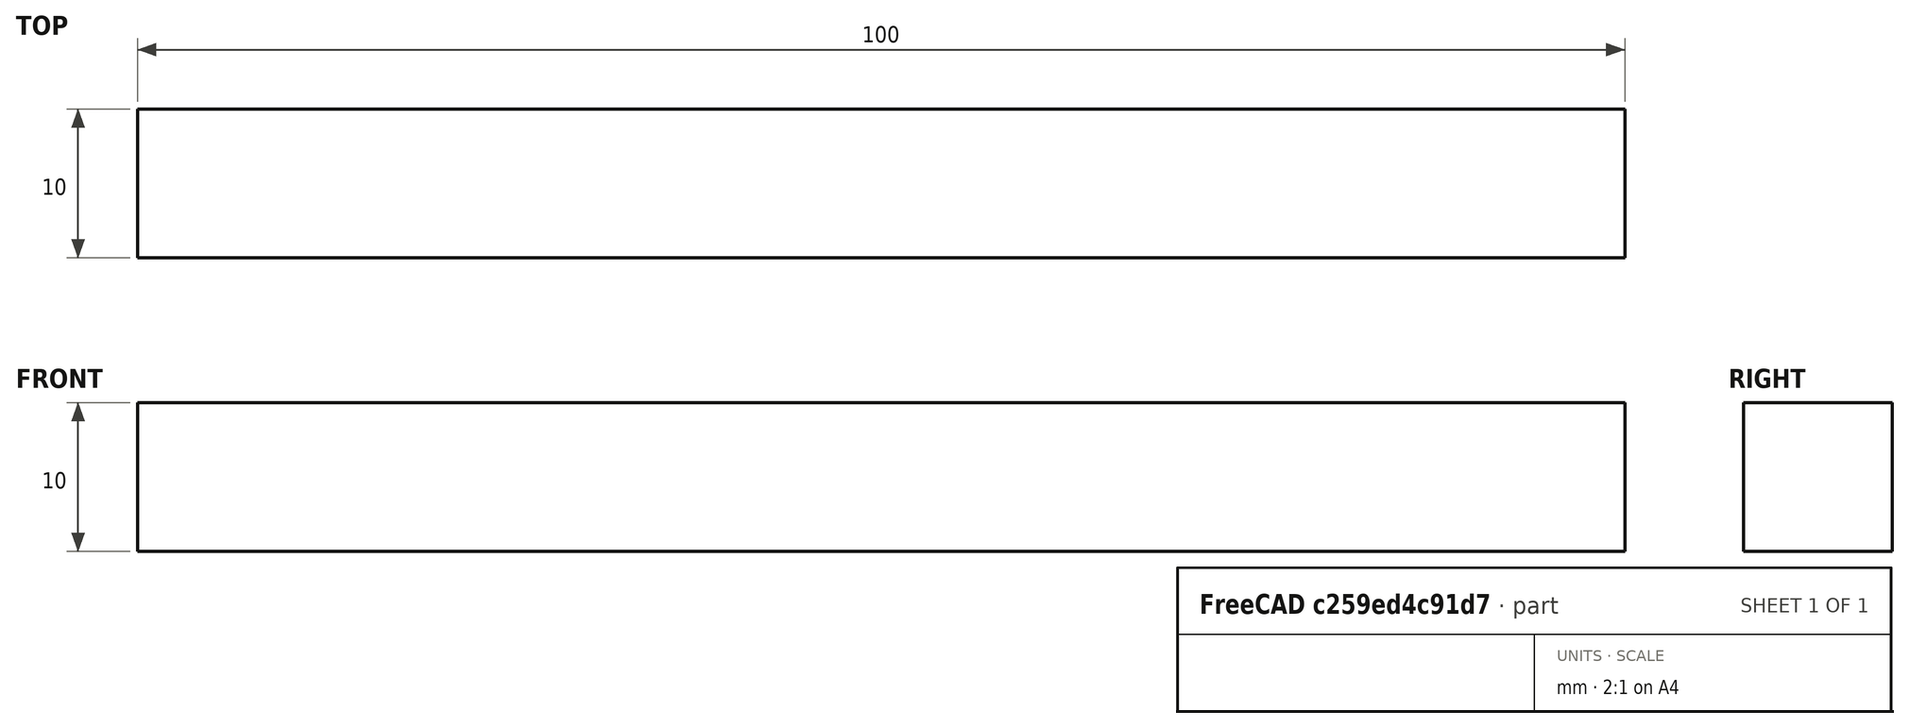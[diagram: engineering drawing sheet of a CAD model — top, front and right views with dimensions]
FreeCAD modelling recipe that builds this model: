
FCSTD DOCUMENT  (FreeCAD 0.21R33694 (Git))
Label: Cantilever
License: All rights reserved
LicenseURL: http://en.wikipedia.org/wiki/All_rights_reserved
objects: Part::Box×1, Fem::ConstraintFixed×1, Fem::ConstraintForce×1, App::MaterialObjectPython×1, Fem::FemSolverObjectPython×1, Fem::FeaturePython×1, Fem::FemMeshObjectPython×1, Fem::FemAnalysis×1
note: 1 computed .brp shape members not serialized (recipe doc carries the construction recipe); baked Part::Feature solids carry a one-line shape summary decoded from their .brp

FEATURE [Part::Box] Box  label="Cube"
  AttacherType = Attacher::AttachEngine3D
  Height = 10
  Length = 100
  Width = 10
FEATURE [Fem::ConstraintFixed] ConstraintFixed
  NormalDirection = (-1,0,0)
  Normals = (9) [(-1,0,0),(-1,0,0),(-1,0,0),(-1,0,0),(-1,0,0),(-1,0,0),(-1,0,0),(-1,0,0),(-1,0,0)]
  Points = (9) [(0,10,0),(0,10,5),(0,10,10),(0,5,0),(0,5,5),(0,5,10),(0,0,0),(0,0,5),(0,0,10)]
  References = -> [Box]
FEATURE [Fem::ConstraintForce] ConstraintForce
  Direction = -> Box [Edge5]
  DirectionVector = (0,0,-1)
  Force = 390
  NormalDirection = (1,0,0)
  Points = (9) [(100,10,0),(100,10,5),(100,10,10),(100,5,0),(100,5,5),(100,5,10),(100,0,0),(100,0,5),(100,0,10)]
  References = -> [Box]
  Reversed = true
FEATURE [App::MaterialObjectPython] MaterialSolid  # material (typed FeaturePython)
  Category = 0
  Material = AuthorAndLicense=(c) 2014 M. Münch - GNU Lesser General Public License (LGPL); CardName=Steel-St-E-315; Density=7800 kg/m^3; Father=Metal; KindOfMaterial=Fine grain steel; KindOfMaterialDE=Feinkornstahl; MaterialNumber=1.0505; Name=St E 315; NameDE=St E 315; Norm=DIN 17102; PoissonRatio=0.3; ShearModulus=81000 MPa; ThermalExpansionCoefficient=0.000011 m/m/K; UltimateStrain=0; UltimateTensileStrength=440 MPa; YieldStrength=320 MPa; YoungsModulus=210000 MPa
FEATURE [Fem::FemSolverObjectPython] SolverCcxTools  # FEM object (typed FeaturePython)
  AnalysisType = 0
  BeamShellResultOutput3D = false
  BucklingFactors = 1
  EigenmodeHighLimit = 1000000
  EigenmodeLowLimit = 0
  EigenmodesCount = 10
  GeometricalNonlinearity = 0
  IterationsControlParameterCutb = 0.25,0.5,0.75,0.85,,,1.5,
  IterationsControlParameterIter = 4,8,9,200,10,400,,200,,
  IterationsControlParameterTimeUse = false
  IterationsThermoMechMaximum = 2000
  IterationsUserDefinedIncrementations = false
  IterationsUserDefinedTimeStepLength = false
  MaterialNonlinearity = 0
  MatrixSolverType = 0
  SplitInputWriter = false
  ThermoMechSteadyState = true
  TimeEnd = 1
  TimeInitialStep = 0.01
FEATURE [Fem::FeaturePython] MeshRegion  # FEM object (typed FeaturePython)
  CharacteristicLength = 0.5
  References = -> [Box]
FEATURE [Fem::FemMeshObjectPython] FEMMeshGmsh  # FEM object (typed FeaturePython)
  Algorithm2D = 0
  Algorithm3D = 0
  CharacteristicLengthMax = 5
  CharacteristicLengthMin = 0
  CoherenceMesh = true
  ElementDimension = 0
  ElementOrder = 1
  GeometryTolerance = 1e-06
  GroupsOfNodes = false
  HighOrderOptimize = 0
  MeshRegionList = -> [MeshRegion]
  MeshSizeFromCurvature = 12
  OptimizeNetgen = false
  OptimizeStd = true
  Part = -> Box
  RecombinationAlgorithm = 0
  Recombine3DAll = false
  RecombineAll = false
  SecondOrderLinear = false
FEATURE [Fem::FemAnalysis] Analysis
  Group = -> [ConstraintFixed,ConstraintForce,MaterialSolid,FEMMeshGmsh,SolverCcxTools]
